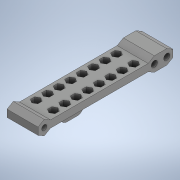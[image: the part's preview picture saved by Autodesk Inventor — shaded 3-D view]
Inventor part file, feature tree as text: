
AUTODESK INVENTOR PART (.ipt)
format: ipt  version: 2020 (Build 240168000, 168)  size: 476,160 bytes
history: native  units: in
note: dims shown in document units (in); Inventor stores cm internally (conversion verified against a paired STEP export)
features: sketch x7, extrude x6, projected_geometry x4, plane x2, mirror x1, fillet x1
ambient origin geometry x8: Origin, YZ Plane, XZ Plane, XY Plane, X Axis, Y Axis, Z Axis, Center Point
bodies: Solid1 (feature_tree)
feature tree (21):
  extrude  "Extrusion1"  Depth=3.4256in
  plane  "Work Plane1"
  extrude  "Extrusion2"  Depth=0.7874in
  sketch  "Sketch4"  dims[d4=0.0in d5=0.0827in]
  extrude  "Extrusion4"  Depth=0.0827in
  plane  "Work Plane2"
  extrude  "Extrusion6"  Depth=3.1106in
  mirror  "Mirror2"
  extrude  "Extrusion7"  Depth=0.315in
  extrude  "Extrusion8"  Depth=0.2362in
  fillet  "Fillet1"  [1 undecoded]
  sketch  "Sketch1"  dims[d0=0.1818in d1=3.4256in]
  sketch  "Sketch2"  dims[d2=0.1339in d3=0.7874in]
  sketch  "Sketch5"  dims[d6=0.7874in d7=0.0in d28=3.1106in]
  sketch  "Sketch7"  dims[d29=0.315in d31=0.315in]
  projected_geometry  "Projected Loop7"
  projected_geometry  "Projected Loop8"
  sketch  "Sketch8"  dims[d33=0.1575in d34=0.2362in d35=0.0in]
  projected_geometry  "Projected Loop9"
  sketch  "Sketch10"  dims[d38=0.315in d39=0.2756in d40=-0.3092in d41=0.0787in d42=0.0787in d43=0.0787in d44=3.1496in d46=0.2913in d47=0.3937in d49=0.3937in d51=3.1496in d53=0.2913in d54=0.3937in d56=0.3937in d58=0.0in d59=0.0in d60=150.0deg d61=0.1339in d63=1.1811in d64=0.1575in d65=0.0in d66=0.126in d67=0.1575in]
  projected_geometry  "Projected Loop10"
note: 1 required parameter value undecoded (feature->parameter linkage not recoverable at this tier; creation-order binding heuristic only, values carry confidence <= 0.55)
